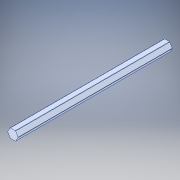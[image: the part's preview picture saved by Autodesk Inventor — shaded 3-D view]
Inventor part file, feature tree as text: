
AUTODESK INVENTOR PART (.ipt)
format: ipt  version: 2017 (Build 210142000, 142)  size: 127,488 bytes
history: native  units: in
note: dims shown in document units (in); Inventor stores cm internally (conversion verified against a paired STEP export)
features: split x1, sketch x1, fillet x1
ambient origin geometry x8: Origin, YZ Plane, XZ Plane, XY Plane, X Axis, Y Axis, Z Axis, Center Point
bodies: Solid1 (feature_tree)
feature tree (3):
  split  "Split1"
  sketch  "Sketch1"
  fillet  "Fillet1"  Radius=8.5in
